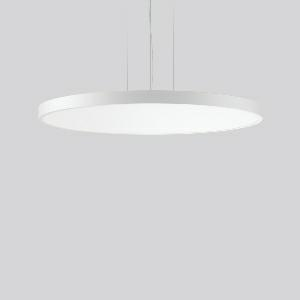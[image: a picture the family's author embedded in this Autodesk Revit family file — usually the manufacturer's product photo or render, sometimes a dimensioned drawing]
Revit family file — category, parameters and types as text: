
# Revit family: triona_round_p_312394_002_76_568b
name_source: partatom
category: Lighting Fixtures
units: mm (PartAtom-declared; Revit-internal decimal feet)

## family parameters
Cut with Voids When Loaded = No
Host = Face
Light Source = No
Part Type = Normal
Room Calculation Point = No
Round Connector Dimension = Use Diameter
Shared = No

## types (1)
- TRIONA round P (1 x LED Modul 830, 15300 lm, 3000)
    Apparent Load = 149 VA
    CIE Flux Codes = 49 80 96 75 100
    Color Rendering = 80
    Color Temperature = 3000
    Default Elevation = 1800 mm
    Description = Series: TRIONA round
Decorative round LED pendant-mounted surface luminaire. Flat, seamless frame: aluminium extrusion profile, powder coated. Cover made of sheet steel, powder-coated. Canopy made of aluminium, powder-coated. Direct light emission through a diffuser plastic opal. Indirect light emission through a flush diffuser made of satin-finish plastic. Lightguide and diffuser made of non-yellowing plastic (PMMA). Lateral light emission (RZB SIDELITE technology) for above-average homogeneous light distribution. Direct 70%, indirect 30% light emission. 3-point steel cable suspension, steplessly adjustable. Easy installation with transparent, adjustable pendant cable and canopy with magnetic fixing. Driver integrated. 
Colour: traffic white, matt (RAL 9016)
Diameter: 1009 mm
Height: 52 mm
Suspension length: 500-1200 mm
Lamp: LED
Socket: without socket
Colour temperature: 3000K
Colour rendering index (CRI): 80
System power: 149 W
Rated luminous flux: 15300 lm
Luminous efficiency: 103 lm/W
Control gear: Converter, dimmable, DALI
Protection class: I
Type of protection: IP 20
    Height = 52 mm
    Lamp = 1 x LED Modul 830
    Lamp Light Flux = 15300 lm
    Lamp count = 1
    Length = 1009 mm
    Lifetime = 50000 h
    Luminous efficacy = 103 lm/W
    Manufacturer = RZB
    ModVariant = No
    Model = 312394.002.76
    Mounting Place = Ceiling
    Mounting Type = Pendant
    Number of Poles = 1
    OnlyDefault = Yes
    Power Factor = 1
    Product Name = TRIONA round P
    Product group = Pendant modular luminaires
    ProductGroupID = 906
    Protection Class = Protection class I
    Protection Degree = IP 20
    RLX_Detail_Level = 1
    RLX_Emergency_Light_Flux = 0 lm
    RLX_Emergency_Type = 0
    RLX_Emergency_Type_DB = No
    RlxData = <blob elided: 38101 chars, md5=fc992df4>
    Socket = socket
    Standby Power = 0 W
    System Light Flux = 15299 lm
    System Power = 149 W
    Type Comments = Product without accessories
    Type Image = 312394.002.jpg
    URL = http://relux.com
    VarID = ---
    Voltage = 230 V
    Voltage Range = 220-240 V
    Weight = 0.00 kg
    Width = 0 mm  [stored 0 ft]

note: [stored X ft] marks values corroborated as IEEE doubles in the binary element streams (Revit-internal decimal feet)

## geometry (parser evidence)
native form markers: Blend x4, Sweep x11
no freeform markers — native parametric forms only
